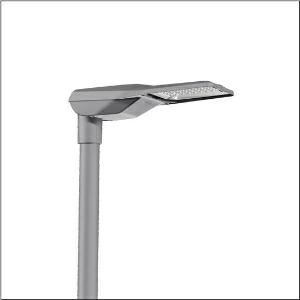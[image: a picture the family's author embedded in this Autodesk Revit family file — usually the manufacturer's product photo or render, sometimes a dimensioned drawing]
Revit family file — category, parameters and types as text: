
# Revit family: streetlight_sl_21_iq_mini___st1_0a_5xe2d31g08gb_f91a
name_source: partatom
category: Lighting Fixtures
units: mm (PartAtom-declared; Revit-internal decimal feet)

## family parameters
Cut with Voids When Loaded = No
Host = Face
Light Source = No
Part Type = Normal
Room Calculation Point = No
Round Connector Dimension = Use Diameter
Shared = No

## types (1)
- --- (1 x LED, 5680 lm, 37.1 W, 3000K)
    Apparent Load = 37 VA
    CIE Flux Codes = 37 72 97 100 100
    Color Rendering = 70
    Color Temperature = 3000K
    Default Elevation = 1800 mm
    Description = Streetlight SL 21 iQ mini, mast luminaire, primary light control with lens, of PMMA, primary optical cover: cover, of toughened safety glass, transparent, light distribution: ST1.0a, light emission: direct distribution, primary light characteristic: asymmetric, installation type: post-top, side-entry, LED, High Power LED, rated luminous flux: 5.680lm, luminous efficacy: 153lm/W, light colour: 730, colour temperature: 3000K, control: Street-Remote, Auto-Match, Temp-Guard, Lumen-Switch, Night-Set, Smart-Wire, Light-Fading, Desk-Remote (wireless, voltage-free reading and setting of iQ features in the workshop via application-optimized NFC function/RFID function), optimised constant luminous flux control (CLO 2.0), pre-setting: linear dimming characteristic, mains connection: 220..240V, AC, 50/60Hz, start of lifetime: 37W, end of service life: 39W, reduction: 18W, luminaire housing, of diecast aluminium, powder-coated, Siteco® metallic grey (DB 702S), corrosivity category C5 mid according to DIN EN ISO 12944, please order mast flange separately, inclination adjustable: 0°, 5°, 10°, 15°, sealing non-destructively replaceable, multi-level sealing system, length: 628mm, width: 235mm, height: 110mm, mast flange for spigot size: 42mm (side-entry): 5XC10008XM4, 60/48mm (side-entry/post-top): 5XC10108XM2, 76/60mm (side-entry/post-top): 5XC10108XM1, protection rating (complete): IP66, insulation class (complete): insulation class II (safety insulation), certification: CE, ENEC, ENEC+, VDE, impact resistance: IK09, permissible operating ambient temperature for outdoor applications: -40..+50°C, standard-compliant lighting for roads and squares, packaging unit: 1 piece

Light Distribution: ST1.0a
    Height = 110 mm
    Lamp = 1 x LED
    Lamp Light Flux = 5680 lm
    Lamp Power = 37.1 W
    Lamp count = 1
    Length = 625 mm
    Luminous efficacy = 153 lm/W
    Manufacturer = Siteco
    ModVariant = No
    Model = 5XE2D31G08GB
    Number of Poles = 1
    OnlyDefault = Yes
    Power Factor = 1
    Product Name = Streetlight SL 21 iQ mini | ST1.0a
    Product group = mast luminaire | pylon top
    ProductGroupID = 6100
    Protection Class = Protection class II
    Protection Degree = IP 66
    RLX_Detail_Level = 1
    RLX_Emergency_Light_Flux = 0 lm
    RLX_Emergency_Type = 0
    RLX_Emergency_Type_DB = No
    RlxData = <blob elided: 92285 chars, md5=fcb6c739>
    Socket = socket
    Standby Power = 0 W
    System Light Flux = 5680 lm
    System Power = 37 W
    Type Comments = factory setting: luminous flux: 100 % | dim-lin: 254 | 385 mA
    Type Image = l_1003519.jpg
    URL = http://relux.com
    VarID = @adj_161031
    Voltage = 0 V
    Weight = 0.00 kg
    Width = 234 mm

## geometry (parser evidence)
native form markers: Blend x4, Sweep x10
no freeform markers — native parametric forms only
